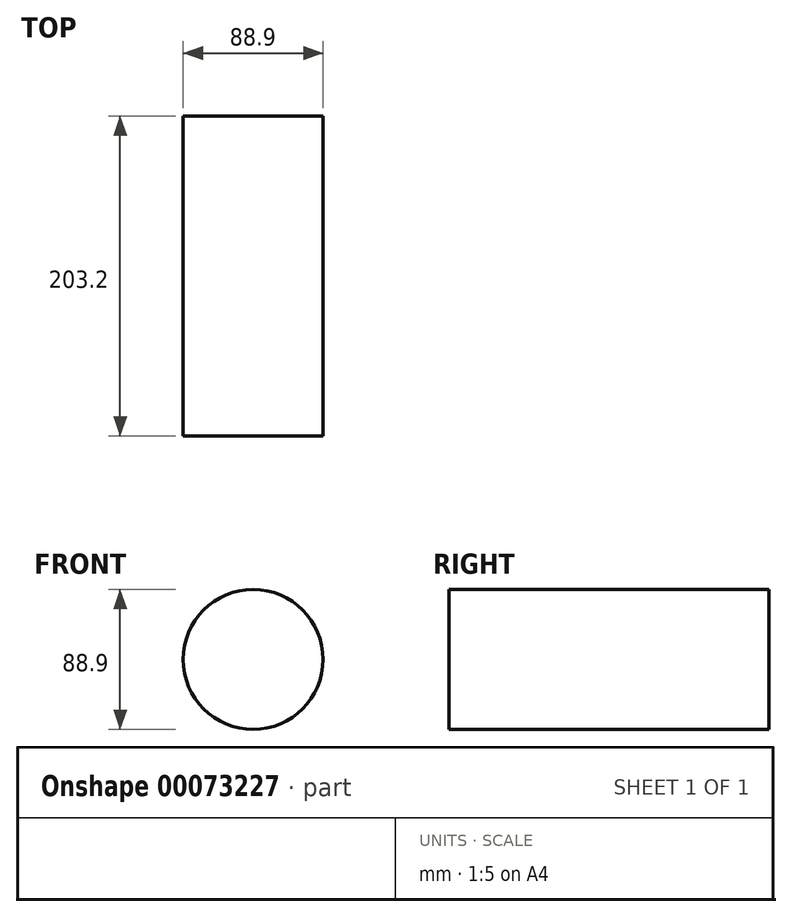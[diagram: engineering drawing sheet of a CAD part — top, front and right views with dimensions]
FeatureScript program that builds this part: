
annotation { "Feature Type Name" : "Feature", "Feature Type Description" : "" }
export const myFeature = defineFeature(function(context is Context, id is Id, definition is map)
    precondition{}
    {
        {
            var Q0;
            Q0=qCreatedBy(makeId("Front.planeOp"),FACE);
            var sketch = newSketch(context, id + "F0", { "sketchPlane" : qUnion([Q0])});
            skCircle(sketch, "E0", {"center": v(0, 0) * mm, "radius": 44.45 * mm});
            skSolve(sketch);
        }
        {
            var Q0;
            Q0 = qSketchRegion(id + "F0", true);
            extrude(context, id + "F1", {"entities" : qUnion([Q0]), "depth" : 203.2 * mm});
        }
    });
